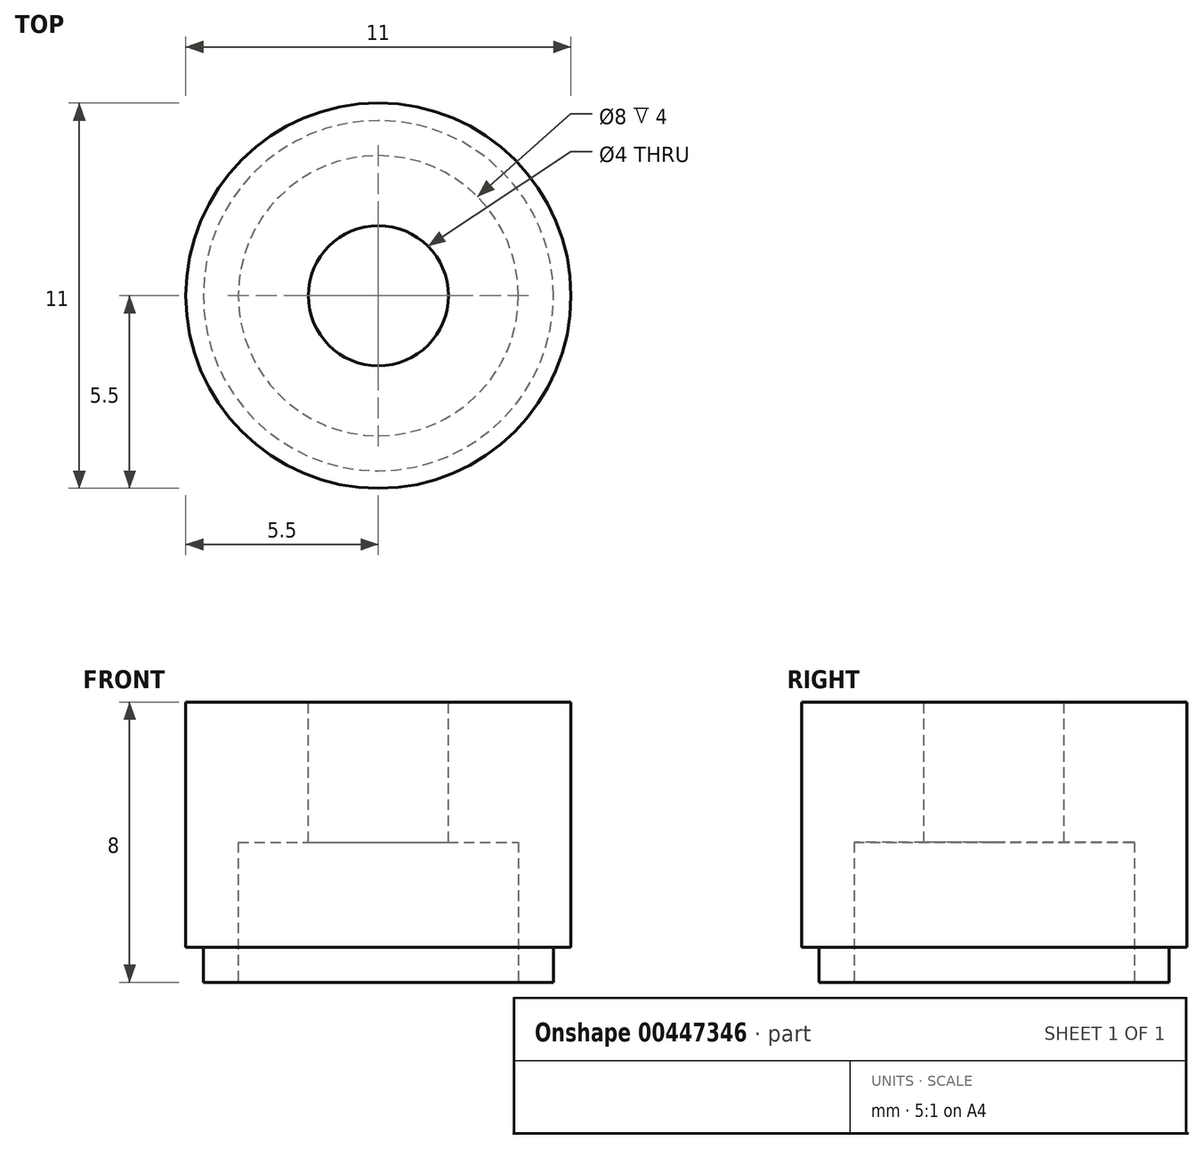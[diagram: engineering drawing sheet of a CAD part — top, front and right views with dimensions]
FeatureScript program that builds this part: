
annotation { "Feature Type Name" : "Feature", "Feature Type Description" : "" }
export const myFeature = defineFeature(function(context is Context, id is Id, definition is map)
    precondition{}
    {
        {
            var Q0;
            Q0=qCreatedBy(makeId("Top.planeOp"),FACE);
            cPlane(context, id + "F0", {"entities" : qUnion([Q0]), "cplaneType" : CPlaneType.OFFSET, "offset" : 4 * mm, "width" : 150 * mm, "height" : 150 * mm});
        }
        {
            var Q0;
            Q0=qCreatedBy(id+"F0.planeOp",FACE);
            var sketch = newSketch(context, id + "F1", { "sketchPlane" : qUnion([Q0])});
            skCircle(sketch, "E0", {"center": v(0, 0) * mm, "radius": 5.5 * mm});
            skSolve(sketch);
        }
        {
            var Q0;
            Q0=makeQuery(id+"F1.imprint","IMPRINT",FACE,{"disambiguationData":[TD([[makeQuery(id+"F1.imprint","IMPRINT",EDGE,{"derivedFrom":sQuery(id+"F1.wireOp",EDGE,"E0")}),1.0]])]});
            extrude(context, id + "F2", {"entities" : qUnion([Q0]), "depth" : 8 * mm, "offsetDistance" : 25 * mm});
        }
        {
            var Q0;
            Q0=makeQuery(id+"F2.opExtrude","CAP_FACE",FACE,{"disambiguationData":[OSD([sQuery(id+"F1.wireOp",EDGE,"E0")])],"isStart":true});
            var sketch = newSketch(context, id + "F3", { "sketchPlane" : qUnion([Q0])});
            skCircle(sketch, "E1", {"center": v(0, 0) * mm, "radius": 4 * mm});
            skSolve(sketch);
        }
        {
            var Q0;
            Q0=makeQuery(id+"F3.imprint","IMPRINT",FACE,{"disambiguationData":[TD([[makeQuery(id+"F3.imprint","IMPRINT",EDGE,{"derivedFrom":sQuery(id+"F3.wireOp",EDGE,"E1")}),1.0]])]});
            extrude(context, id + "F4", {"entities" : qUnion([Q0]), "operationType" : NewBodyOperationType.REMOVE, "oppositeDirection" : true, "depth" : 4 * mm});
        }
        {
            var Q0;
            Q0=makeQuery(id+"F2.opExtrude","CAP_FACE",FACE,{"disambiguationData":[OSD([sQuery(id+"F1.wireOp",EDGE,"E0")])],"isStart":false});
            var sketch = newSketch(context, id + "F5", { "sketchPlane" : qUnion([Q0])});
            skCircle(sketch, "E2", {"center": v(0, 0) * mm, "radius": 2 * mm});
            skCircle(sketch, "E3", {"center": v(0, 0) * mm, "radius": 1 * mm});
            skSolve(sketch);
        }
        {
            var Q0;
            Q0=makeQuery(id+"F5.imprint","IMPRINT",FACE,{"disambiguationData":[TD([[makeQuery(id+"F5.imprint","IMPRINT",EDGE,{"derivedFrom":sQuery(id+"F5.wireOp",EDGE,"E3")}),1.0]])]});
            extrude(context, id + "F6", {"entities" : qUnion([Q0]), "operationType" : NewBodyOperationType.REMOVE, "oppositeDirection" : true, "depth" : 25 * mm});
        }
        {
            var Q0;
            Q0=makeQuery(id+"F5.imprint","IMPRINT",FACE,{"disambiguationData":[TD([[makeQuery(id+"F5.imprint","IMPRINT",EDGE,{"derivedFrom":sQuery(id+"F5.wireOp",EDGE,"E2")}),1.0]])]});
            extrude(context, id + "F7", {"entities" : qUnion([Q0]), "operationType" : NewBodyOperationType.REMOVE, "oppositeDirection" : true, "depth" : 5 * mm});
        }
        {
            var Q0;
            Q0=makeQuery(id+"F2.opExtrude","CAP_FACE",FACE,{"disambiguationData":[OSD([sQuery(id+"F1.wireOp",EDGE,"E0")])],"isStart":true});
            var sketch = newSketch(context, id + "F8", { "sketchPlane" : qUnion([Q0])});
            skCircle(sketch, "E4.0", {"center": v(0, 0) * mm, "radius": 5 * mm});
            skSolve(sketch);
        }
        {
            var Q0;
            Q0=makeQuery(id+"F8.imprint","IMPRINT",FACE,{"disambiguationData":[TD([[makeQuery(id+"F8.imprint","IMPRINT",EDGE,{"derivedFrom":sQuery(id+"F8.wireOp",EDGE,"E4.0")}),-1.0]])]});
            extrude(context, id + "F9", {"entities" : qUnion([Q0]), "operationType" : NewBodyOperationType.REMOVE, "oppositeDirection" : true, "depth" : 1 * mm, "offsetDistance" : 25 * mm});
        }
    });
